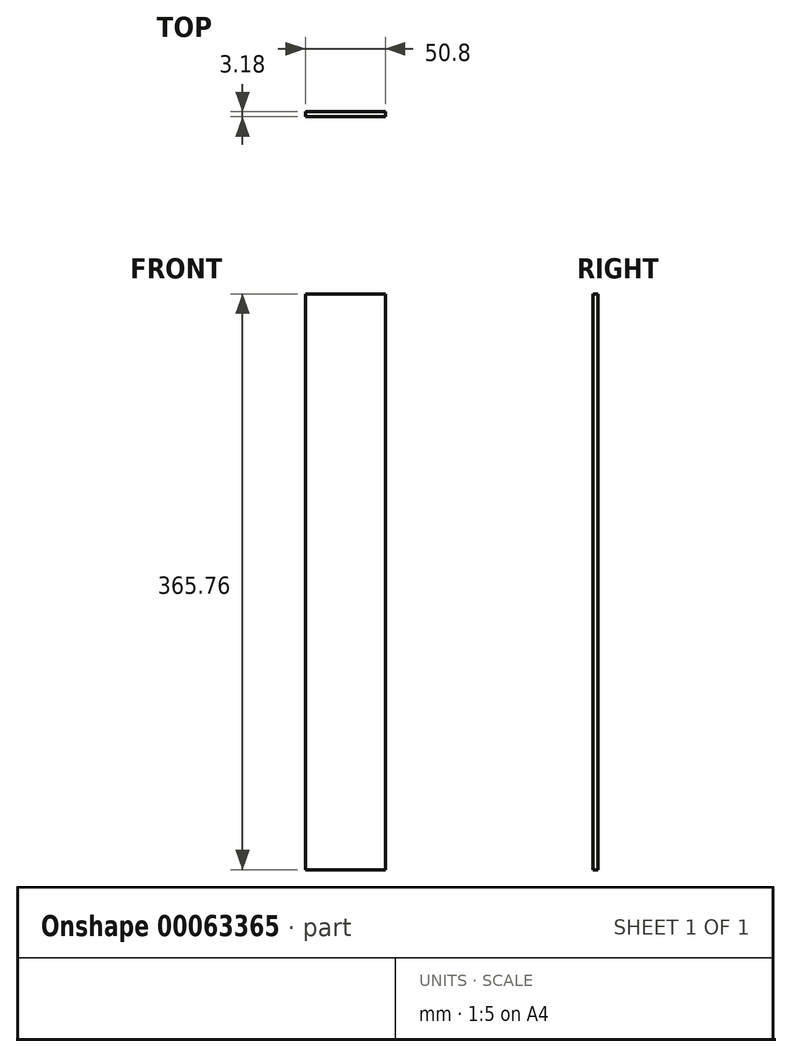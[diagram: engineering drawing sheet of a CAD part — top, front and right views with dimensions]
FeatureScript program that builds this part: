
annotation { "Feature Type Name" : "Feature", "Feature Type Description" : "" }
export const myFeature = defineFeature(function(context is Context, id is Id, definition is map)
    precondition{}
    {
        {
            var Q0;
            Q0=qCreatedBy(makeId("Front.planeOp"),FACE);
            var sketch = newSketch(context, id + "F0", { "sketchPlane" : qUnion([Q0])});
            skLineSegment(sketch, "E0.rect.bottom", {"start": v(25.4, 182.88) * mm, "end": v(-25.4, 182.88) * mm});
            skLineSegment(sketch, "E0.rect.top", {"start": v(25.4, -182.88) * mm, "end": v(-25.4, -182.88) * mm});
            skLineSegment(sketch, "E0.rect.left", {"start": v(25.4, 182.88) * mm, "end": v(25.4, -182.88) * mm});
            skLineSegment(sketch, "E0.rect.right", {"start": v(-25.4, 182.88) * mm, "end": v(-25.4, -182.88) * mm});
            skPoint(sketch, "E0.rect.middle", {"position": v(0, 0) * mm});
            skSolve(sketch);
        }
        {
            var Q0;
            Q0=makeQuery(id+"F0.imprint","IMPRINT",FACE,{"disambiguationData":[TD([[makeQuery(id+"F0.imprint","IMPRINT",EDGE,{"derivedFrom":sQuery(id+"F0.wireOp",EDGE,"E0.rect.bottom")}),1.0]])]});
            extrude(context, id + "F1", {"entities" : qUnion([Q0]), "endBound" : BoundingType.SYMMETRIC, "depth" : 3.17 * mm});
        }
    });
